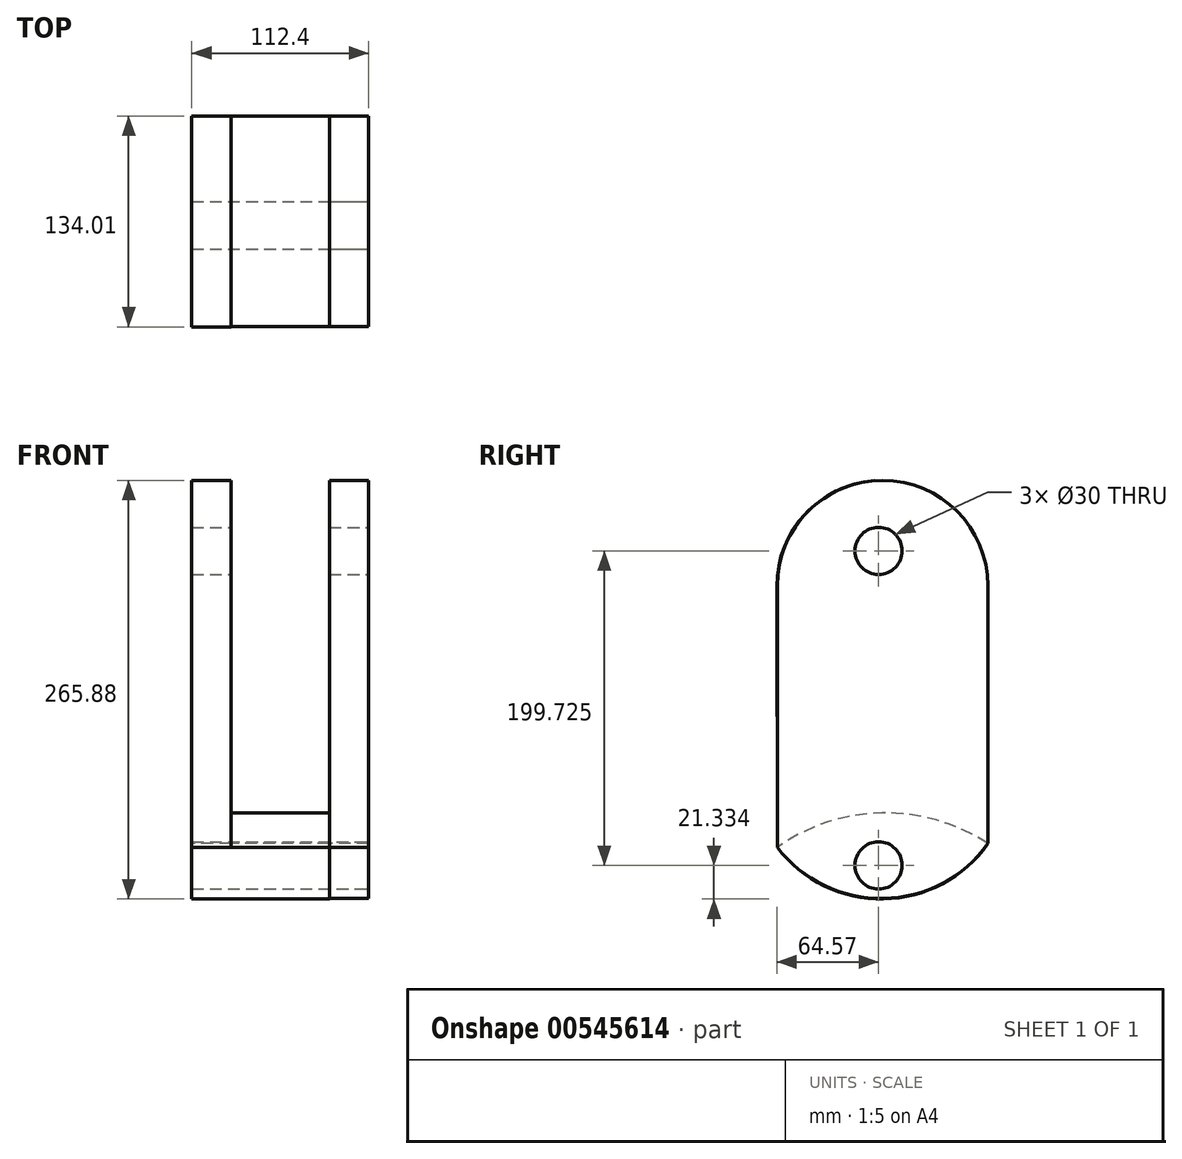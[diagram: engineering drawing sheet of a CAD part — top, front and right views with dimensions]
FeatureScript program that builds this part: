
annotation { "Feature Type Name" : "Feature", "Feature Type Description" : "" }
export const myFeature = defineFeature(function(context is Context, id is Id, definition is map)
    precondition{}
    {
        {
            var Q0;
            Q0=qCreatedBy(makeId("Right.planeOp"),FACE);
            var sketch = newSketch(context, id + "F0", { "sketchPlane" : qUnion([Q0])});
            skArc(sketch, "E0", {"start": v(69.44, -19.62) * mm, "mid": v(2.22, -0.13) * mm, "end": v(-64.29, -21.9) * mm});
            skArc(sketch, "E1", {"start": v(-64.29, -21.9) * mm, "mid": v(3.16, -54.77) * mm, "end": v(69.44, -19.62) * mm});
            skSolve(sketch);
        }
        {
            var Q0;
            Q0=makeQuery(id+"F0.imprint","IMPRINT",FACE,{"disambiguationData":[TD([[makeQuery(id+"F0.imprint","IMPRINT",EDGE,{"derivedFrom":sQuery(id+"F0.wireOp",EDGE,"E0")}),1.0]])]});
            extrude(context, id + "F1", {"entities" : qUnion([Q0]), "depth" : 87.4 * mm, "offsetDistance" : 25 * mm, "symmetric" : true});
        }
        {
            var Q0;
            Q0=makeQuery(id+"F1.opExtrude","CAP_FACE",FACE,{"disambiguationData":[OSD([sQuery(id+"F0.wireOp",EDGE,"E0"),sQuery(id+"F0.wireOp",EDGE,"E1")])],"isStart":false});
            var sketch = newSketch(context, id + "F2", { "sketchPlane" : qUnion([Q0])});
            skArc(sketch, "E2", {"start": v(-64.29, -21.9) * mm, "mid": v(3.15, -54.47) * mm, "end": v(69.44, -19.62) * mm});
            skLineSegment(sketch, "E3", {"start": v(-64.29, -21.9) * mm, "end": v(-64.29, 144.23) * mm});
            skLineSegment(sketch, "E4", {"start": v(69.44, -19.62) * mm, "end": v(69.44, 144.23) * mm});
            skArc(sketch, "E5", {"start": v(69.44, 144.23) * mm, "mid": v(2.58, 211.1) * mm, "end": v(-64.29, 144.23) * mm});
            skSolve(sketch);
        }
        {
            var Q0;
            Q0=makeQuery(id+"F1.opExtrude","CAP_FACE",FACE,{"disambiguationData":[OSD([sQuery(id+"F0.wireOp",EDGE,"E0"),sQuery(id+"F0.wireOp",EDGE,"E1")])],"isStart":true});
            var sketch = newSketch(context, id + "F3", { "sketchPlane" : qUnion([Q0])});
            skArc(sketch, "E6", {"start": v(-69.44, -19.62) * mm, "mid": v(-3.16, -54.68) * mm, "end": v(64.29, -21.9) * mm});
            skLineSegment(sketch, "E7", {"start": v(-69.44, -19.62) * mm, "end": v(-69.44, 144.51) * mm});
            skLineSegment(sketch, "E8", {"start": v(64.57, 143.97) * mm, "end": v(64.29, -21.9) * mm});
            skArc(sketch, "E9", {"start": v(64.57, 143.97) * mm, "mid": v(-2.17, 211.09) * mm, "end": v(-69.44, 144.51) * mm});
            skSolve(sketch);
        }
        {
            var Q0;
            Q0=makeQuery(id+"F2.imprint","IMPRINT",FACE,{"disambiguationData":[TD([[makeQuery(id+"F2.imprint","IMPRINT",EDGE,{"derivedFrom":sQuery(id+"F2.wireOp",EDGE,"E3")}),-1.0]])]});
            var Q1;
            Q1=makeQuery(id+"F2.imprint","IMPRINT",FACE,{"disambiguationData":[TD([[makeQuery(id+"F2.imprint","IMPRINT",EDGE,{"derivedFrom":sQuery(id+"F2.wireOp",EDGE,"E2")}),1.0]])]});
            var Q2;
            Q2=makeQuery(id+"F3.imprint","IMPRINT",FACE,{"disambiguationData":[TD([[makeQuery(id+"F3.imprint","IMPRINT",EDGE,{"derivedFrom":sQuery(id+"F3.wireOp",EDGE,"E6")}),1.0]])]});
            var Q3;
            Q3=makeQuery(id+"F3.imprint","IMPRINT",FACE,{"disambiguationData":[TD([[makeQuery(id+"F3.imprint","IMPRINT",EDGE,{"derivedFrom":sQuery(id+"F3.wireOp",EDGE,"E7")}),-1.0]])]});
            extrude(context, id + "F4", {"entities" : qUnion([Q0, Q1, Q2, Q3]), "operationType" : NewBodyOperationType.ADD, "depth" : 25 * mm, "offsetDistance" : 25 * mm});
        }
        {
            var Q0;
            Q0=makeQuery(id+"F4.opExtrude","CAP_FACE",FACE,{"disambiguationData":[OSD([sQuery(id+"F2.wireOp",EDGE,"E2"),sQuery(id+"F2.wireOp",EDGE,"E3"),sQuery(id+"F2.wireOp",EDGE,"E4"),sQuery(id+"F2.wireOp",EDGE,"E5")])],"isStart":false});
            var sketch = newSketch(context, id + "F5", { "sketchPlane" : qUnion([Q0])});
            skCircle(sketch, "E10", {"center": v(0, -33.45) * mm, "radius": 13.47 * mm});
            skCircle(sketch, "E11", {"center": v(0, 166.28) * mm, "radius": 17.07 * mm});
            skSolve(sketch);
        }
        {
            var Q0;
            Q0=sQuery(id+"F5.wireOp",VERTEX,"E10.center");
            var Q1;
            Q1=makeQuery(id+"F1.opExtrude","SWEPT_BODY",BODY,{"disambiguationData":[OSD([sQuery(id+"F0.wireOp",EDGE,"E0"),sQuery(id+"F0.wireOp",EDGE,"E1")])]});
            hole(context, id + "F6", {"style" : HoleStyle.SIMPLE, "endStyle" : HoleEndStyle.THROUGH, "holeDiameter" : 30 * mm, "majorDiameter" : 5 * mm, "isTappedThrough" : true, "tappedDepth" : 12 * mm, "tapClearance" : 3, "locations" : qUnion([Q0]), "scope" : qUnion([Q1])});
        }
        {
            var Q0;
            Q0=makeQuery(id+"F4.opExtrude","CAP_FACE",FACE,{"disambiguationData":[OSD([sQuery(id+"F2.wireOp",EDGE,"E2"),sQuery(id+"F2.wireOp",EDGE,"E3"),sQuery(id+"F2.wireOp",EDGE,"E4"),sQuery(id+"F2.wireOp",EDGE,"E5")])],"isStart":false});
            var sketch = newSketch(context, id + "F7", { "sketchPlane" : qUnion([Q0])});
            skCircle(sketch, "E12", {"center": v(0, 166.28) * mm, "radius": 14.35 * mm});
            skSolve(sketch);
        }
        {
            var Q0;
            Q0=sQuery(id+"F7.wireOp",VERTEX,"E12.center");
            var Q1;
            Q1=makeQuery(id+"F1.opExtrude","SWEPT_BODY",BODY,{"disambiguationData":[OSD([sQuery(id+"F0.wireOp",EDGE,"E0"),sQuery(id+"F0.wireOp",EDGE,"E1")])]});
            hole(context, id + "F8", {"style" : HoleStyle.SIMPLE, "endStyle" : HoleEndStyle.THROUGH, "holeDiameter" : 30 * mm, "majorDiameter" : 5 * mm, "isTappedThrough" : true, "tappedDepth" : 12 * mm, "tapClearance" : 3, "locations" : qUnion([Q0]), "scope" : qUnion([Q1])});
        }
    });
